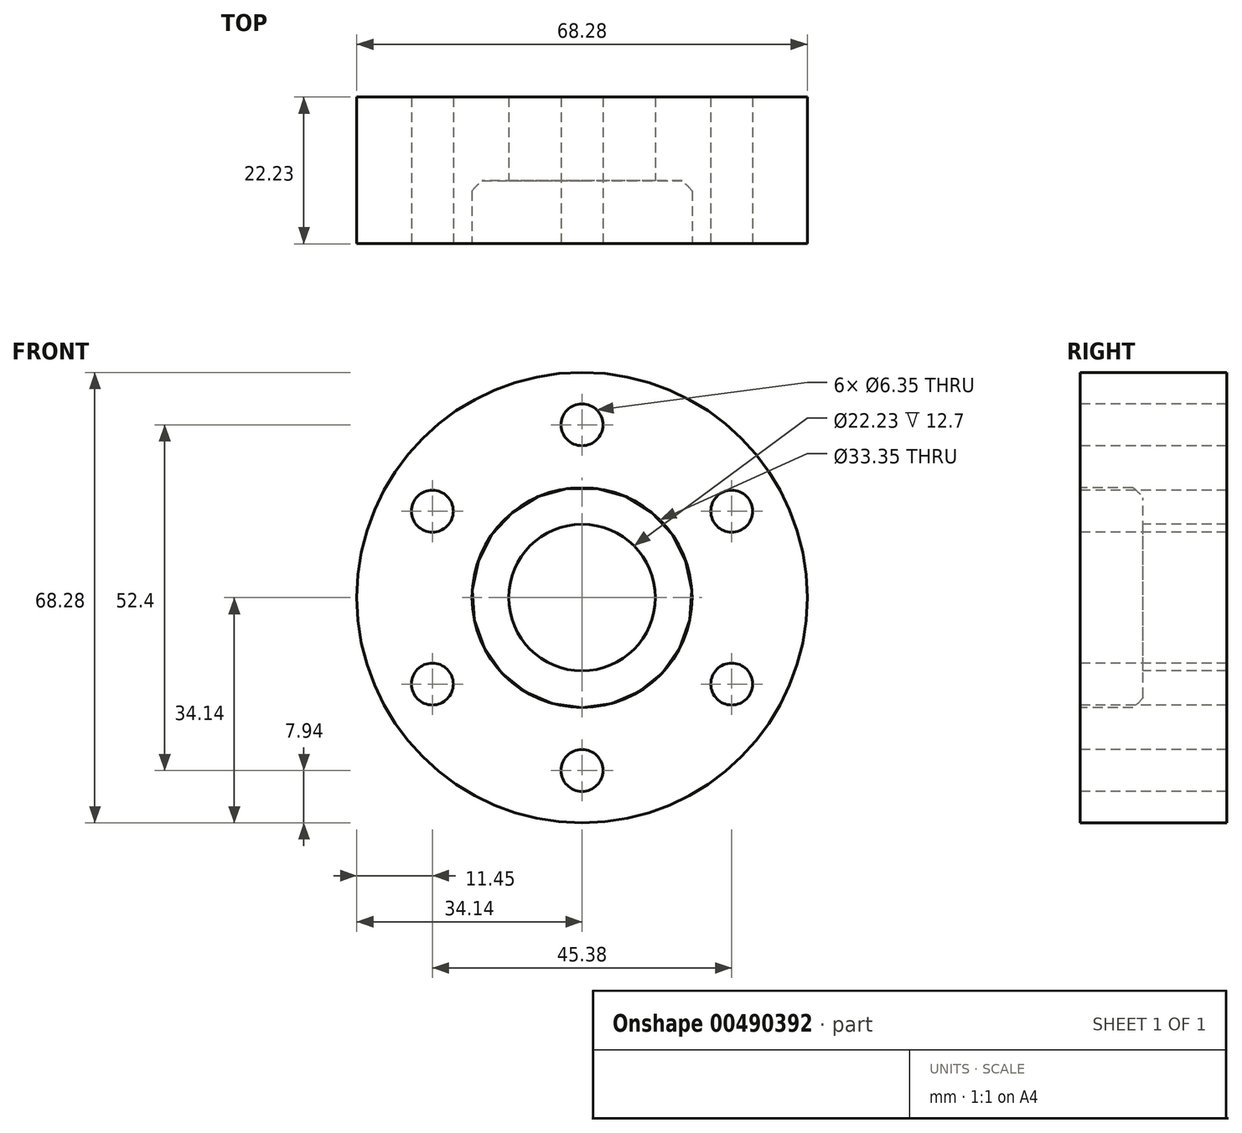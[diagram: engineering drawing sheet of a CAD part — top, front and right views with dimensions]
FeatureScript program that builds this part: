
annotation { "Feature Type Name" : "Feature", "Feature Type Description" : "" }
export const myFeature = defineFeature(function(context is Context, id is Id, definition is map)
    precondition{}
    {
        {
            var Q0;
            Q0=qCreatedBy(makeId("Front.planeOp"),FACE);
            var sketch = newSketch(context, id + "F0", { "sketchPlane" : qUnion([Q0])});
            skCircle(sketch, "E0", {"center": v(0, 0) * mm, "radius": 34.14 * mm});
            skCircle(sketch, "E1", {"center": v(0, 0) * mm, "radius": 26.2 * mm, "construction": true});
            skSolve(sketch);
        }
        {
            var Q0;
            Q0 = qSketchRegion(id + "F0", true);
            extrude(context, id + "F1", {"entities" : qUnion([Q0]), "depth" : 22.22 * mm});
        }
        {
            var Q0;
            Q0=makeQuery(id+"F1.opExtrude","CAP_FACE",FACE,{"disambiguationData":[OSD([sQuery(id+"F0.wireOp",EDGE,"E0")])],"isStart":false});
            var sketch = newSketch(context, id + "F2", { "sketchPlane" : qUnion([Q0])});
            skCircle(sketch, "E2", {"center": v(0, 0) * mm, "radius": 11.11 * mm});
            skLineSegment(sketch, "E3", {"start": v(0, 65.47) * mm, "end": v(0, -63.84) * mm, "construction": true});
            skSolve(sketch);
        }
        {
            var Q0;
            Q0 = qSketchRegion(id + "F2", true);
            extrude(context, id + "F3", {"entities" : qUnion([Q0]), "operationType" : NewBodyOperationType.REMOVE, "endBound" : BoundingType.THROUGH_ALL, "oppositeDirection" : true, "depth" : 25.4 * mm});
        }
        {
            var Q0;
            Q0=makeQuery(id+"F1.opExtrude","CAP_FACE",FACE,{"disambiguationData":[OSD([sQuery(id+"F0.wireOp",EDGE,"E0")])],"isStart":false});
            var sketch = newSketch(context, id + "F4", { "sketchPlane" : qUnion([Q0])});
            skLineSegment(sketch, "E4", {"start": v(0, 59.76) * mm, "end": v(0, -69.62) * mm, "construction": true});
            skCircle(sketch, "E5", {"center": v(0, 0) * mm, "radius": 26.2 * mm, "construction": true});
            skCircle(sketch, "E6", {"center": v(0, -26.2) * mm, "radius": 3.18 * mm});
            skLineSegment(sketch, "E7", {"start": v(-60.3, 34.81) * mm, "end": v(0, 0) * mm, "construction": true});
            skLineSegment(sketch, "E8", {"start": v(0, 0) * mm, "end": v(76.4, -44.1) * mm, "construction": true});
            skLineSegment(sketch, "E9", {"start": v(63.76, 36.8) * mm, "end": v(0, 0) * mm, "construction": true});
            skLineSegment(sketch, "E10", {"start": v(0, 0) * mm, "end": v(-57.7, -33.31) * mm, "construction": true});
            skCircle(sketch, "E11", {"center": v(22.69, -13.1) * mm, "radius": 3.18 * mm});
            skCircle(sketch, "E12", {"center": v(0, 26.2) * mm, "radius": 3.18 * mm});
            skCircle(sketch, "E13", {"center": v(22.69, 13.1) * mm, "radius": 3.18 * mm});
            skCircle(sketch, "E14", {"center": v(-22.69, -13.1) * mm, "radius": 3.18 * mm});
            skCircle(sketch, "E15", {"center": v(-22.69, 13.1) * mm, "radius": 3.18 * mm});
            skSolve(sketch);
        }
        {
            var Q0;
            Q0 = qSketchRegion(id + "F4", true);
            extrude(context, id + "F5", {"entities" : qUnion([Q0]), "operationType" : NewBodyOperationType.REMOVE, "endBound" : BoundingType.THROUGH_ALL, "oppositeDirection" : true, "depth" : 25.4 * mm});
        }
        {
            var Q0;
            Q0=makeQuery(id+"F1.opExtrude","CAP_FACE",FACE,{"disambiguationData":[OSD([sQuery(id+"F0.wireOp",EDGE,"E0")])],"isStart":false});
            var sketch = newSketch(context, id + "F6", { "sketchPlane" : qUnion([Q0])});
            skCircle(sketch, "E16", {"center": v(0, 0) * mm, "radius": 16.68 * mm});
            skSolve(sketch);
        }
        {
            var Q0;
            Q0 = qSketchRegion(id + "F6", true);
            extrude(context, id + "F7", {"entities" : qUnion([Q0]), "operationType" : NewBodyOperationType.REMOVE, "oppositeDirection" : true, "depth" : 9.52 * mm});
        }
        {
            var Q0;
            Q0=makeQuery(id+"F7.boolean.opBoolean","COPY",EDGE,{"derivedFrom":makeQuery(id+"F7.opExtrude","CAP_EDGE",EDGE,{"disambiguationData":[OSD([sQuery(id+"F6.wireOp",EDGE,"E16")])],"isStart":false})});
            fillet(context, id + "F8", {"entities" : qUnion([Q0]), "radius" : 1.52 * mm, "tangentPropagation" : true, "rho" : 0.06, "crossSection" : FilletCrossSection.CONIC, "allowEdgeOverflow" : false});
        }
    });
